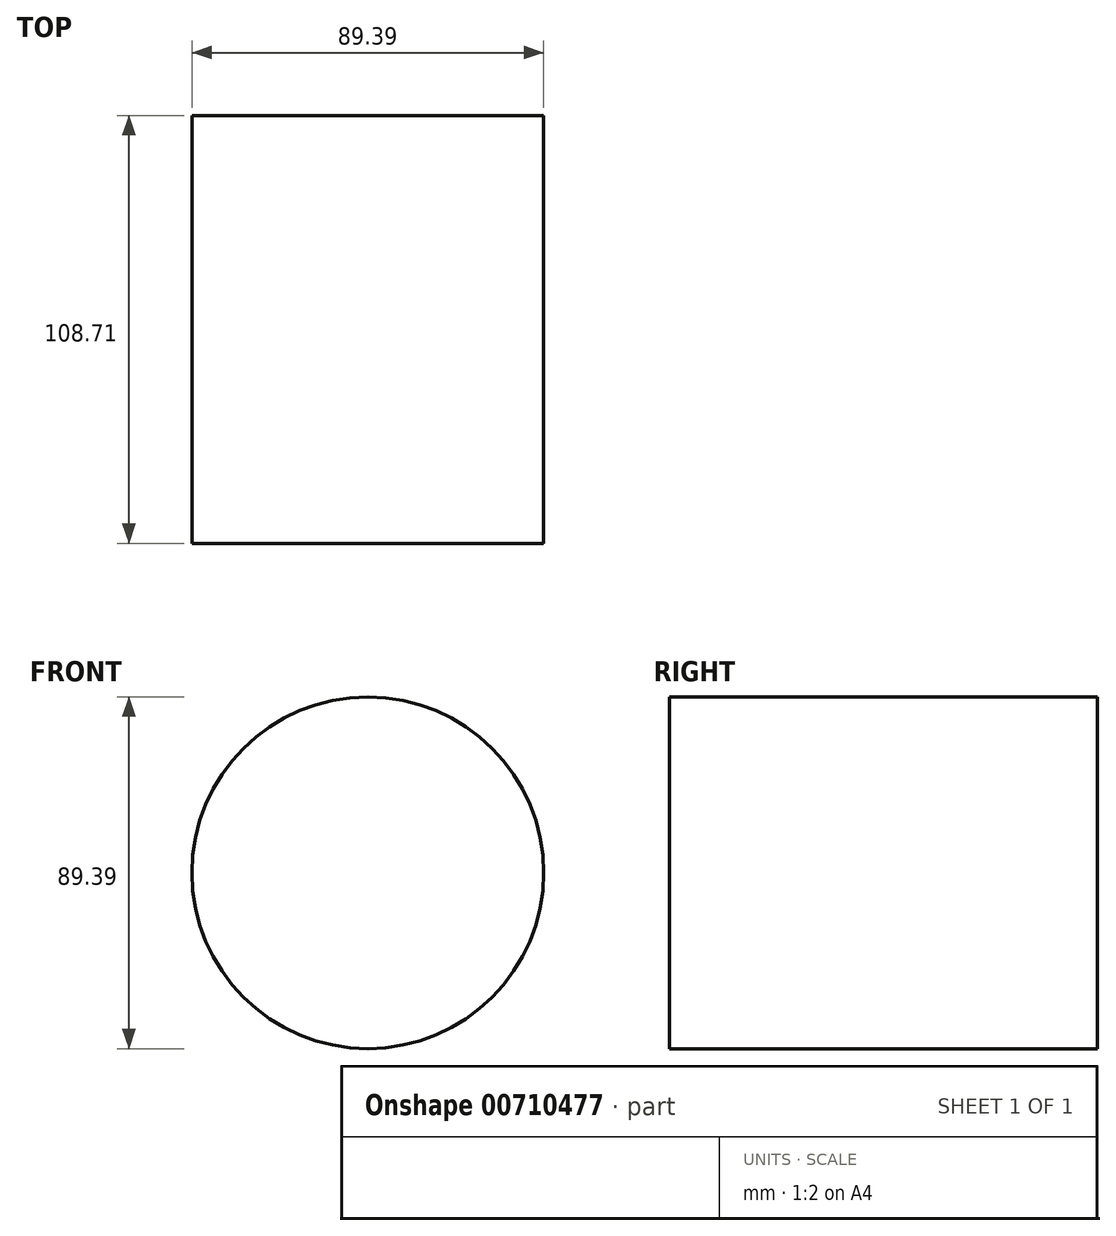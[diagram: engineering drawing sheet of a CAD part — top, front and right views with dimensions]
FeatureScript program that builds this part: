
annotation { "Feature Type Name" : "Feature", "Feature Type Description" : "" }
export const myFeature = defineFeature(function(context is Context, id is Id, definition is map)
    precondition{}
    {
        {
            var Q0;
            Q0=qCreatedBy(makeId("Front.planeOp"),FACE);
            var sketch = newSketch(context, id + "F0", { "sketchPlane" : qUnion([Q0])});
            skCircle(sketch, "E0", {"center": v(-16.95, 11.1) * mm, "radius": 44.7 * mm});
            skSolve(sketch);
        }
        {
            var Q0;
            Q0=makeQuery(id+"F0.imprint","IMPRINT",FACE,{"disambiguationData":[TD([[makeQuery(id+"F0.imprint","IMPRINT",EDGE,{"derivedFrom":sQuery(id+"F0.wireOp",EDGE,"E0")}),1.0]])]});
            extrude(context, id + "F1", {"entities" : qUnion([Q0]), "depth" : 108.7 * mm, "offsetDistance" : 25.4 * mm});
        }
    });
